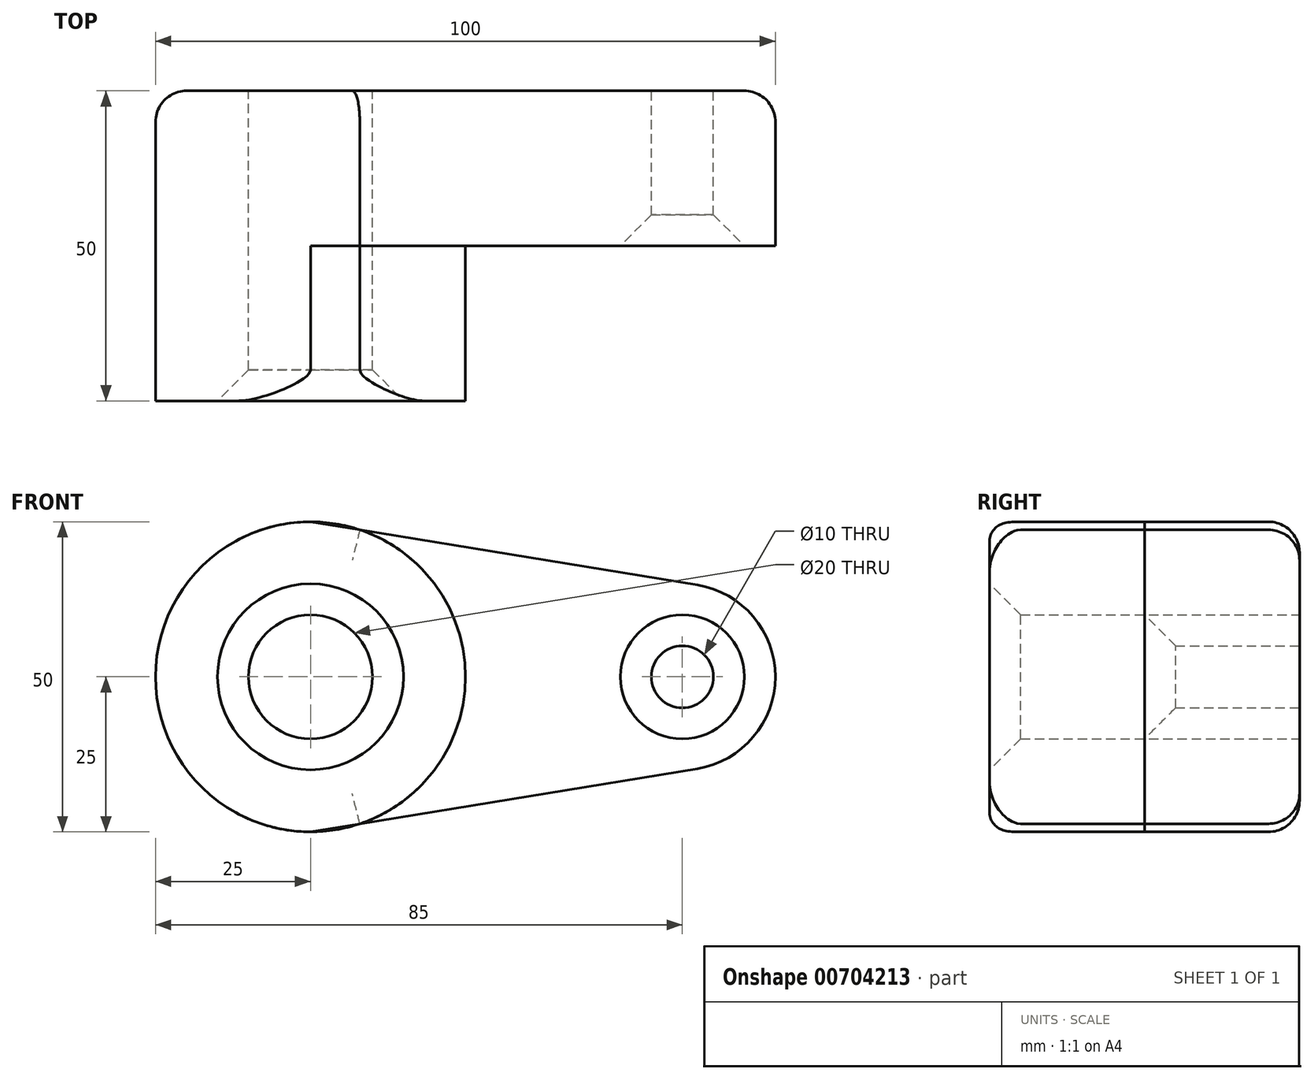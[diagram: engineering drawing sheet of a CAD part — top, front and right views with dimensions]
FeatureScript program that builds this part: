
annotation { "Feature Type Name" : "Feature", "Feature Type Description" : "" }
export const myFeature = defineFeature(function(context is Context, id is Id, definition is map)
    precondition{}
    {
        {
            var Q0;
            Q0=qCreatedBy(makeId("Front.planeOp"),FACE);
            var sketch = newSketch(context, id + "F0", { "sketchPlane" : qUnion([Q0])});
            skCircle(sketch, "E0", {"center": v(0, 0) * mm, "radius": 25 * mm});
            skCircle(sketch, "E1", {"center": v(60, 0) * mm, "radius": 15 * mm});
            skLineSegment(sketch, "E2", {"start": v(0, 25) * mm, "end": v(62.42, 14.8) * mm});
            skLineSegment(sketch, "E3", {"start": v(0, -25) * mm, "end": v(62.42, -14.8) * mm});
            skCircle(sketch, "E4", {"center": v(0, 0) * mm, "radius": 10 * mm});
            skCircle(sketch, "E5", {"center": v(60, 0) * mm, "radius": 5 * mm});
            skSolve(sketch);
        }
        {
            var Q0;
            Q0 = qSketchRegion(id + "F0", true);
            extrude(context, id + "F1", {"entities" : qUnion([Q0]), "depth" : 25 * mm, "offsetDistance" : 25 * mm});
        }
        {
            var Q0;
            Q0=makeQuery(id+"F0.imprint","IMPRINT",FACE,{"disambiguationData":[TD([[makeQuery(id+"F0.imprint","IMPRINT",EDGE,{"derivedFrom":sQuery(id+"F0.wireOp",EDGE,"E4")}),-1.0]])]});
            extrude(context, id + "F2", {"entities" : qUnion([Q0]), "operationType" : NewBodyOperationType.ADD, "depth" : 50 * mm, "offsetDistance" : 25 * mm});
        }
        {
            var Q0;
            {var subQ0=sQuery(id+"F0.wireOp",EDGE,"E0");Q0=makeQuery(id+"F2.opExtrude","CAP_EDGE",EDGE,{"disambiguationData":[OSD([subQ0]),TDD([makeQuery(id+"F0.imprint","IMPRINT",EDGE,{"disambiguationData":[TD([[makeQuery(id+"F0.imprint","INTERSECT",VERTEX,{"disambiguationData":[OD(0.0)],"derivedFrom":[subQ0,sQuery(id+"F0.wireOp",EDGE,"E2")]}),-1.0]])],"derivedFrom":subQ0})])],"isStart":false});}
            var Q1;
            Q1=makeQuery(id+"F2.opExtrude","CAP_EDGE",EDGE,{"disambiguationData":[OSD([sQuery(id+"F0.wireOp",EDGE,"E3")])],"isStart":false});
            var Q2;
            {var subQ0=sQuery(id+"F0.wireOp",EDGE,"E0");Q2=makeQuery(id+"F2.opExtrude","CAP_EDGE",EDGE,{"disambiguationData":[OSD([subQ0]),TDD([makeQuery(id+"F0.imprint","IMPRINT",EDGE,{"disambiguationData":[TD([[makeQuery(id+"F0.imprint","INTERSECT",VERTEX,{"disambiguationData":[OD(1.0)],"derivedFrom":[subQ0,sQuery(id+"F0.wireOp",EDGE,"E2")]}),1.0]])],"derivedFrom":subQ0})])],"isStart":false});}
            var Q3;
            Q3=makeQuery(id+"F2.opExtrude","CAP_EDGE",EDGE,{"disambiguationData":[OSD([sQuery(id+"F0.wireOp",EDGE,"E2")])],"isStart":false});
            var Q4;
            Q4=makeQuery(id+"F1.opExtrude","CAP_EDGE",EDGE,{"disambiguationData":[OSD([sQuery(id+"F0.wireOp",EDGE,"E3")])],"isStart":true});
            var Q5;
            Q5=makeQuery(id+"F1.opExtrude","CAP_EDGE",EDGE,{"disambiguationData":[OSD([sQuery(id+"F0.wireOp",EDGE,"E0")])],"isStart":true});
            fillet(context, id + "F3", {"entities" : qUnion([Q0, Q1, Q2, Q3, Q4, Q5]), "radius" : 5 * mm, "tangentPropagation" : true, "allowEdgeOverflow" : false});
        }
        {
            var Q0;
            Q0=makeQuery(id+"F2.opExtrude","CAP_EDGE",EDGE,{"disambiguationData":[OSD([sQuery(id+"F0.wireOp",EDGE,"E4")])],"isStart":false});
            var Q1;
            Q1=makeQuery(id+"F1.opExtrude","CAP_EDGE",EDGE,{"disambiguationData":[OSD([sQuery(id+"F0.wireOp",EDGE,"E5")])],"isStart":false});
            chamfer(context, id + "F4", {"entities" : qUnion([Q0, Q1]), "width" : 5 * mm, "tangentPropagation" : true});
        }
    });
